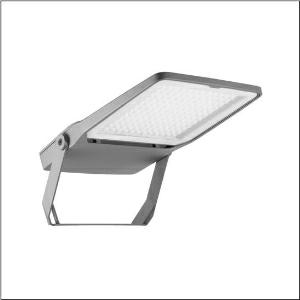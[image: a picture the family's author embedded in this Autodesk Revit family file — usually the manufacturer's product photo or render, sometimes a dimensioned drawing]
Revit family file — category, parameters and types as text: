
# Revit family: floodlight_fl_20_midi___pl61_5xa7682e1c1ac_6874
name_source: partatom
category: Lighting Fixtures
units: mm (PartAtom-declared; Revit-internal decimal feet)

## family parameters
Cut with Voids When Loaded = No
Host = Face
Light Source = No
Part Type = Normal
Room Calculation Point = No
Round Connector Dimension = Use Diameter
Shared = No

## types (1)
- --- (1 x LED 3000K / CRI = 80 (unbekannt), 21280 lm, 3000K)
    Apparent Load = 208 VA
    CIE Flux Codes = 33 65 98 100 100
    Color Rendering = 80
    Color Temperature = 3000K
    Default Elevation = 1800 mm
    Description = Floodlight FL 20 midi, floodlight, primary light control with lens, of plastic, primary optical cover: protective disc, of toughened safety glass, transparent, light distribution: PL61, light emission: direct distribution, primary light characteristic: asymmetric, installation type: surface-mounted, LED, High Power LED, rated luminous flux: 21.280lm, luminous efficacy: 102lm/W, light colour: 830, colour temperature: 3000K, control gear: ECG Plus, control: flexible luminous flux parameterisation, time-dependent luminous flux control, digital communication interface, power reduction, overheat protection, electronic power reduction, with terminal, 5-pole, max. 2.5mm², mains connection: 220..240V, AC, 50/60Hz, rated input power: 208W, LED unit, of diecast aluminium, powder-coated, Siteco® metallic grey (DB 702S), corrosivity category C5 mid according to DIN EN ISO 12944, incl. 1x M20 cable gland for cable Ø 6.5..12mm, length: 654mm, width: 450mm, height: 76mm, housing frame, of diecast aluminium, powder-coated, Siteco® metallic grey (DB 702S), mounting bracket, of steel, powder-coated, Siteco® metallic grey (DB 702S), DALI, protection rating (complete): IP66, insulation class (complete): insulation class II (safety insulation), certification: CE, ENEC, VDE, protection symbol: D, permissible operating ambient temperature: -40..+40°C, permissible operating ambient temperature for outdoor applications: -40..+50°C, standard: DIN EN 12944, packaging unit: 1 piece

Light Distribution: PL61
    Height = 76 mm
    Lamp = 1 x LED 3000K / CRI >= 80 (unbekannt)
    Lamp Light Flux = 21280 lm
    Lamp count = 1
    Length = 672 mm
    Luminous efficacy = 102 lm/W
    Manufacturer = Siteco
    ModVariant = No
    Model = 5XA7682E1C1AC
    Mounting Place = Wall
    Mounting Type = Surface mounted
    Number of Poles = 1
    OnlyDefault = Yes
    Power Factor = 1
    Product Name = Floodlight FL 20 midi | PL61
    Product group = floodlight | wall mounted
    ProductGroupID = 2001
    Protection Class = Protection class II
    Protection Degree = IP 66
    RLX_Detail_Level = 1
    RLX_Emergency_Light_Flux = 0 lm
    RLX_Emergency_Type = 0
    RLX_Emergency_Type_DB = No
    RlxData = <blob elided: 98189 chars, md5=fd36ccbd>
    Socket = socket
    Standby Power = 0 W
    System Light Flux = 21280 lm
    System Power = 208 W
    Type Comments = factory setting: luminous flux: 100 % | dim-lin: 254 | 484 mA
    Type Image = l_1005943.jpg
    URL = http://relux.com
    VarID = @adj_147063
    Voltage = 0 V
    Weight = 0.00 kg
    Width = 450 mm

## geometry (parser evidence)
native form markers: Blend x4, Sweep x12
no freeform markers — native parametric forms only
